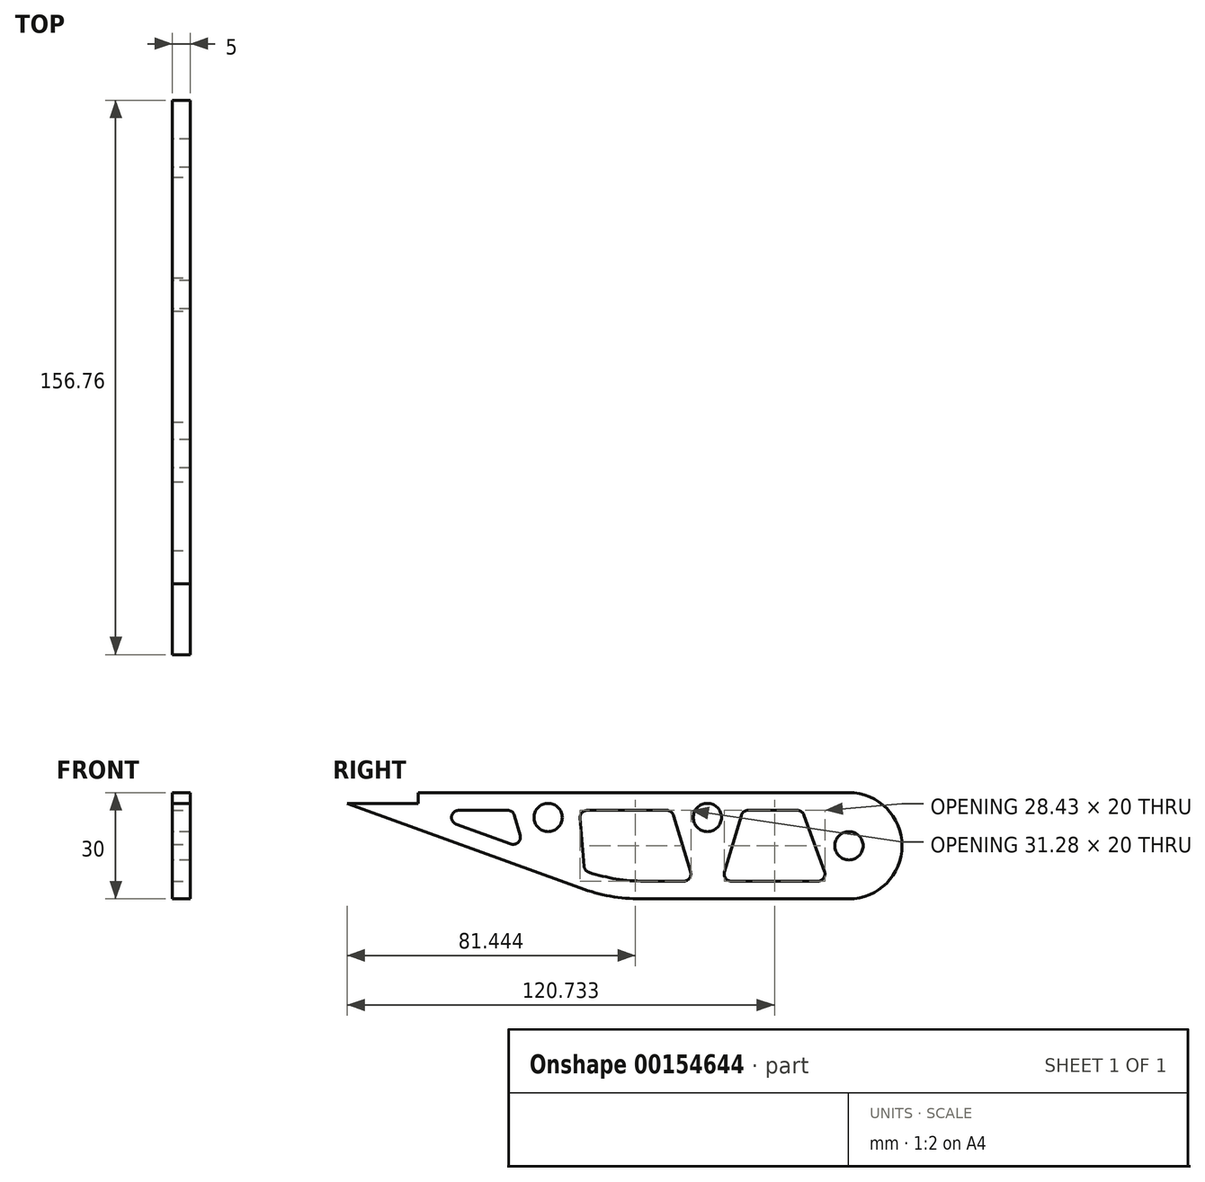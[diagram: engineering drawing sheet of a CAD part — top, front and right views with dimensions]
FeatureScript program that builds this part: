
annotation { "Feature Type Name" : "Feature", "Feature Type Description" : "" }
export const myFeature = defineFeature(function(context is Context, id is Id, definition is map)
    precondition{}
    {
        {
            var Q0;
            Q0=qCreatedBy(makeId("Right.planeOp"),FACE);
            var sketch = newSketch(context, id + "F0", { "sketchPlane" : qUnion([Q0])});
            skLineSegment(sketch, "E0.bottom", {"start": v(-71.76, 15) * mm, "end": v(50, 15) * mm});
            skLineSegment(sketch, "E0.top", {"start": v(-8.76, -15) * mm, "end": v(50, -15) * mm});
            skArc(sketch, "E1", {"start": v(50, -15) * mm, "mid": v(65, 0) * mm, "end": v(50, 15) * mm});
            skLineSegment(sketch, "E2", {"start": v(-91.76, 12) * mm, "end": v(-25.86, -11.98) * mm});
            skCircle(sketch, "E3", {"center": v(50, 0) * mm, "radius": 4 * mm});
            skPoint(sketch, "E4.visualSharp", {"position": v(-17.58, -15) * mm});
            skArc(sketch, "E4.filletArc", {"start": v(-25.86, -11.98) * mm, "mid": v(-17.44, -14.24) * mm, "end": v(-8.76, -15) * mm});
            skPoint(sketch, "E5.visualSharp", {"position": v(-100, 15) * mm});
            skCircle(sketch, "E6", {"center": v(10, 8) * mm, "radius": 4 * mm});
            skCircle(sketch, "E7", {"center": v(-35, 8) * mm, "radius": 4 * mm});
            skLineSegment(sketch, "E8.top", {"start": v(-71.76, 12) * mm, "end": v(-91.76, 12) * mm});
            skLineSegment(sketch, "E8.left", {"start": v(-71.76, 15) * mm, "end": v(-71.76, 12) * mm});
            skSolve(sketch);
        }
        {
            var Q0;
            Q0=qSketchRegion(id+"F0",true);
            extrude(context, id + "F1", {"entities" : qUnion([Q0]), "depth" : 5 * mm});
        }
        {
            var Q0;
            Q0=makeQuery(id+"F1.opExtrude","CAP_FACE",FACE,{"disambiguationData":[OSD([sQuery(id+"F0.wireOp",EDGE,"E0.bottom"),sQuery(id+"F0.wireOp",EDGE,"E0.top"),sQuery(id+"F0.wireOp",EDGE,"E1"),sQuery(id+"F0.wireOp",EDGE,"E2"),sQuery(id+"F0.wireOp",EDGE,"E3"),sQuery(id+"F0.wireOp",EDGE,"E4.filletArc"),sQuery(id+"F0.wireOp",EDGE,"E5.filletArc"),sQuery(id+"F0.wireOp",EDGE,"E6")])],"isStart":false});
            var sketch = newSketch(context, id + "F2", { "sketchPlane" : qUnion([Q0])});
            skLineSegment(sketch, "E9", {"start": v(-23.96, 10) * mm, "end": v(-1.49, 10) * mm});
            skLineSegment(sketch, "E10", {"start": v(0.43, 8.58) * mm, "end": v(5.24, -7.42) * mm});
            skLineSegment(sketch, "E11", {"start": v(14.84, -7.43) * mm, "end": v(19.55, 8.57) * mm});
            skLineSegment(sketch, "E12", {"start": v(21.47, 10) * mm, "end": v(35.4, 10) * mm});
            skLineSegment(sketch, "E13", {"start": v(16.75, -10) * mm, "end": v(41.2, -10) * mm});
            skLineSegment(sketch, "E14", {"start": v(43.08, -7.32) * mm, "end": v(37.28, 8.68) * mm});
            skPoint(sketch, "E15.visualSharp", {"position": v(44.05, -10) * mm});
            skArc(sketch, "E15.filletArc", {"start": v(41.2, -10) * mm, "mid": v(42.84, -9.15) * mm, "end": v(43.08, -7.32) * mm});
            skPoint(sketch, "E16.visualSharp", {"position": v(36.8, 10) * mm});
            skArc(sketch, "E16.filletArc", {"start": v(37.28, 8.68) * mm, "mid": v(36.55, 9.64) * mm, "end": v(35.4, 10) * mm});
            skPoint(sketch, "E17.visualSharp", {"position": v(19.97, 10) * mm});
            skArc(sketch, "E17.filletArc", {"start": v(21.47, 10) * mm, "mid": v(20.27, 9.6) * mm, "end": v(19.55, 8.57) * mm});
            skPoint(sketch, "E18.visualSharp", {"position": v(14.08, -10) * mm});
            skArc(sketch, "E18.filletArc", {"start": v(14.84, -7.43) * mm, "mid": v(15.15, -9.2) * mm, "end": v(16.75, -10) * mm});
            skPoint(sketch, "E19.visualSharp", {"position": v(4.75, -5.8) * mm});
            skPoint(sketch, "E20.visualSharp", {"position": v(0, 10) * mm});
            skArc(sketch, "E20.filletArc", {"start": v(0.43, 8.58) * mm, "mid": v(-0.3, 9.6) * mm, "end": v(-1.49, 10) * mm});
            skPoint(sketch, "E21.visualSharp", {"position": v(-26.13, 10) * mm});
            skLineSegment(sketch, "E22", {"start": v(-7.88, -10) * mm, "end": v(3.33, -10) * mm});
            skPoint(sketch, "E23.visualSharp", {"position": v(-16.7, -10) * mm});
            skArc(sketch, "E23.filletArc", {"start": v(-23.46, -7.5) * mm, "mid": v(-15.77, -9.37) * mm, "end": v(-7.88, -10) * mm});
            skPoint(sketch, "E24.visualSharp", {"position": v(6.02, -10) * mm});
            skArc(sketch, "E24.filletArc", {"start": v(3.33, -10) * mm, "mid": v(4.93, -9.2) * mm, "end": v(5.24, -7.42) * mm});
            skLineSegment(sketch, "E25", {"start": v(-25.96, 7.84) * mm, "end": v(-24.83, -5.77) * mm});
            skPoint(sketch, "E26.visualSharp", {"position": v(-24.72, -7.08) * mm});
            skArc(sketch, "E26.filletArc", {"start": v(-24.83, -5.77) * mm, "mid": v(-24.4, -6.85) * mm, "end": v(-23.46, -7.5) * mm});
            skArc(sketch, "E27.filletArc", {"start": v(-23.96, 10) * mm, "mid": v(-25.43, 9.35) * mm, "end": v(-25.96, 7.84) * mm});
            skLineSegment(sketch, "E28", {"start": v(-46.4, 10) * mm, "end": v(-60.3, 10) * mm});
            skLineSegment(sketch, "E29", {"start": v(-60.99, 6.12) * mm, "end": v(-45.55, 0.5) * mm});
            skLineSegment(sketch, "E30", {"start": v(-42.94, 2.91) * mm, "end": v(-44.48, 8.53) * mm});
            skPoint(sketch, "E31.visualSharp", {"position": v(-41.91, -0.82) * mm});
            skArc(sketch, "E31.filletArc", {"start": v(-45.55, 0.5) * mm, "mid": v(-43.5, 0.91) * mm, "end": v(-42.94, 2.91) * mm});
            skPoint(sketch, "E32.visualSharp", {"position": v(-44.88, 10) * mm});
            skArc(sketch, "E32.filletArc", {"start": v(-44.48, 8.53) * mm, "mid": v(-45.2, 9.6) * mm, "end": v(-46.4, 10) * mm});
            skPoint(sketch, "E33.visualSharp", {"position": v(-71.64, 10) * mm});
            skArc(sketch, "E33.filletArc", {"start": v(-60.3, 10) * mm, "mid": v(-62.27, 8.35) * mm, "end": v(-60.99, 6.12) * mm});
            skSolve(sketch);
        }
        {
            var Q0;
            Q0 = qSketchRegion(id + "F2", true);
            extrude(context, id + "F3", {"entities" : qUnion([Q0]), "operationType" : NewBodyOperationType.REMOVE, "oppositeDirection" : true, "depth" : 25 * mm});
        }
    });
